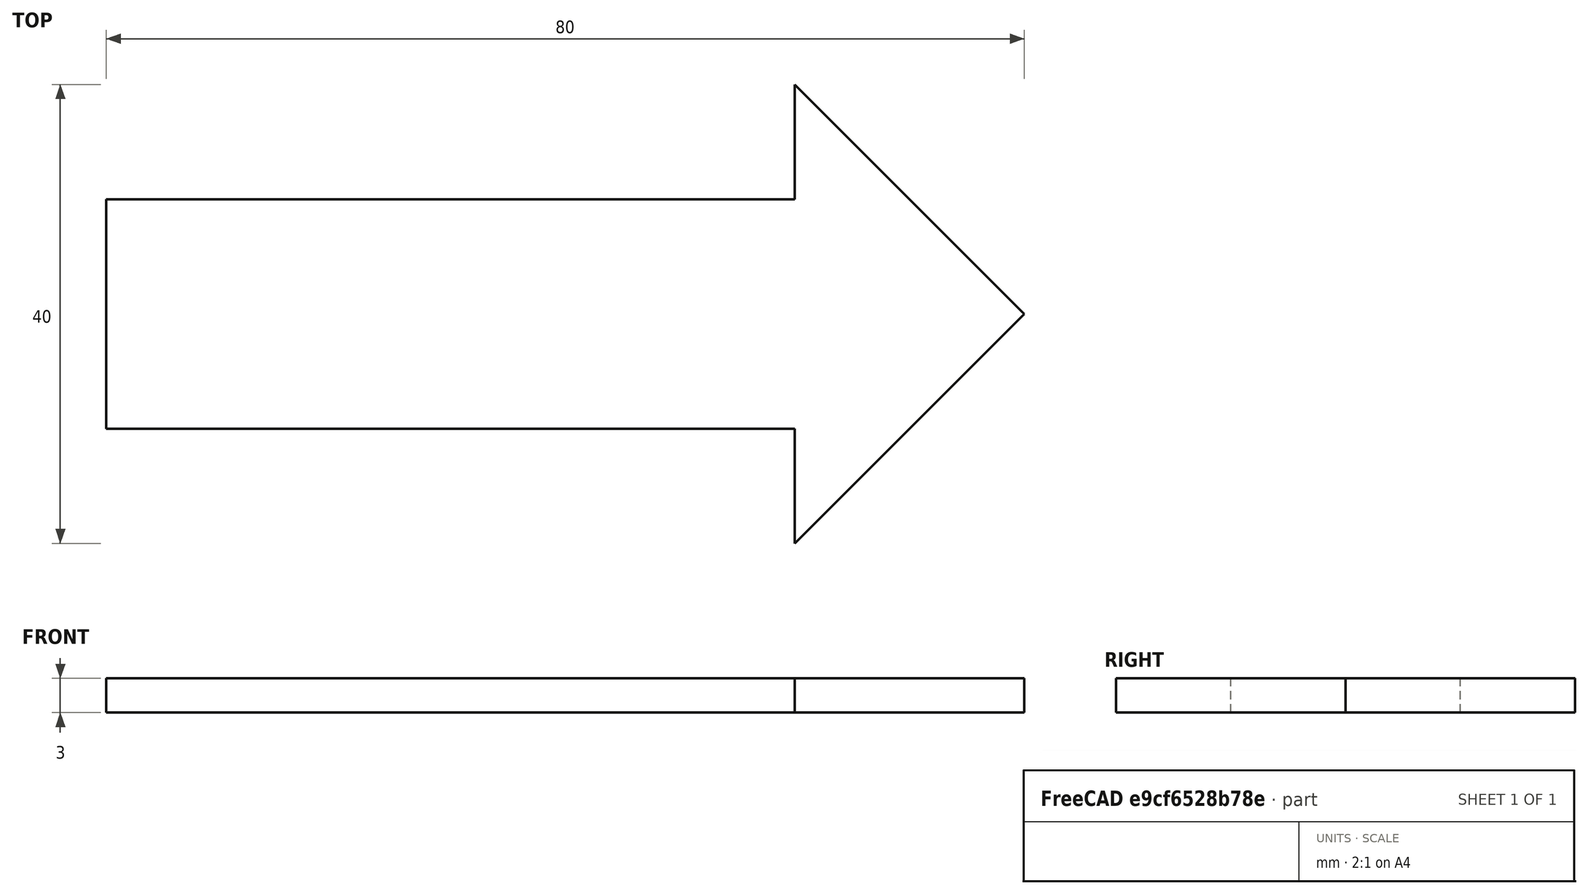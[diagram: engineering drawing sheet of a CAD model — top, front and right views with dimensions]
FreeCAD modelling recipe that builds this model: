
FCSTD DOCUMENT  (FreeCAD 0.18.4R)
Label: tutorial_freecad_ex16_c
License: All rights reserved
LicenseURL: http://en.wikipedia.org/wiki/All_rights_reserved
objects: Sketcher::SketchObject×1, PartDesign::Pad×1, PartDesign::Body×1
note: 4 computed .brp shape members not serialized (recipe doc carries the construction recipe); baked Part::Feature solids carry a one-line shape summary decoded from their .brp

FEATURE [Sketcher::SketchObject] Sketch  label="boceto_flecha"
  MapMode = 5
  Support = -> [XY_Plane]
  sketch-geometry (7):
    g0: LineSegment StartX=-20 StartY=10 StartZ=0 EndX=40 EndY=10 EndZ=0
    g1: LineSegment StartX=40 StartY=10 StartZ=0 EndX=40 EndY=20 EndZ=0
    g2: LineSegment StartX=40 StartY=20 StartZ=0 EndX=60 EndY=0 EndZ=0
    g3: LineSegment StartX=60 StartY=0 StartZ=0 EndX=40 EndY=-20 EndZ=0
    g4: LineSegment StartX=40 StartY=-20 StartZ=0 EndX=40 EndY=-10 EndZ=0
    g5: LineSegment StartX=40 StartY=-10 StartZ=0 EndX=-20 EndY=-10 EndZ=0
    g6: LineSegment StartX=-20 StartY=-10 StartZ=0 EndX=-20 EndY=10 EndZ=0
  constraints (7):
    c: Coincident(g0,g1)
    c: Coincident(g1,g2)
    c: Coincident(g2,g3)
    c: Coincident(g3,g4)
    c: Coincident(g4,g5)
    c: Coincident(g5,g6)
    c: Coincident(g6,g0)
FEATURE [PartDesign::Pad] Pad  label="pad_flecha"
  Length = 3
  Length2 = 100
  Profile = -> Sketch
  Refine = true
  Type = 0
FEATURE [PartDesign::Body] Body  label="flecha"
  Group = -> [Sketch,Pad]
  Origin = -> Origin
  Tip = -> Pad
